# Revit family: elupura s wall hung wc 540 rimless aquahelix flush, hygieneeffect
name_source: partatom
category: Plumbing Fixtures
units: mm (PartAtom-declared; Revit-internal decimal feet)

## family parameters
Always vertical = Yes
Cut with Voids When Loaded = No
OmniClass Number = 23.45.00.00
OmniClass Title = Sanitary, Laundry, and Cleaning Equipment
Part Type = Valve - Breaks Into
Room Calculation Point = No
Round Connector Dimension = Use Diameter
Shared = Yes
Work Plane-Based = No

## types (2) — shared parameters
ARTNR = 62024450
BASENUMBER = 62024
BIMOBJECT = Sanitary: Toilets
CATALOG = Hansgrohe
CNSPipeRound/CP_Outlet_V = No
CNSPipeRound/CP_inlet_V = No
COLLECTION = toilets
COLLECTIONSET = EluPura S
DEPTH = 540
DESIGN = Germany
GTINCODE = 4059625420959
HEIGHT = 400
IDNR = 1
IFC = Furnishing element
Manufacturer = Hansgrohe
NAME = EluPura S Wall hung WC 540 rimless AquaHelix Flush, HygieneEffect
NBSYN = $BASENUMBER.-$ARTNR.-$SURFACE.-$LODLEVEL.
NN = EluPura S Wall hung WC 540 rimless AquaHelix Flush, HygieneEffect
OBJECTTYPE = Object (single object)
OMNICLASS = 23-31 19 00 | Toilets
PERMALINK = 62024XXX
PRODUCTURL = https://pro.hansgrohe.com
REGION = Worldwide
SPECIFICATION = Surfaces:  - 62024450 White   Specification:  • material: ceramic  • HygieneEffect - reduces the spread of coliform bacteria and salmonella (Escherichia coli ATCC8739/Salmonella enterica ATCC 13076. Test: ISO 22196: 2011-08) • Made to fit NoiseReduction: customized soundproofing mat included • degree of gloss: glossy  • AquaHelix Flush: Water vortex technology for optimal flushing • flushing type: wash-down  • rimless • concealed fastening • horizontal outlet • installation type: wall-mounted
SURFACE = GLOSSY_WHITE
UNICLASS2015 = Pr_40_20_93_94 | WC pans
UNICLASS_2015_CODE = 40_20_93_94
WEIGHT = 22
WIDTH = 360

## per-type parameters (varying)
| type | LODLEVEL |
| 62024-62024450-GLOSSY_WHITE-200 | 200 |
| 62024-62024450-GLOSSY_WHITE-400 | 400 |

note: column(s) folded — value = type name in every type: LINA, Model, NB

type visibility flags: 2 boolean params named "<type name>_RX0RY0RZ0TX0TY0TZ0_V" — each type sets only its own to Yes (folded from table)

## geometry (parser evidence)
native form markers: Sweep x19
no freeform markers — native parametric forms only
